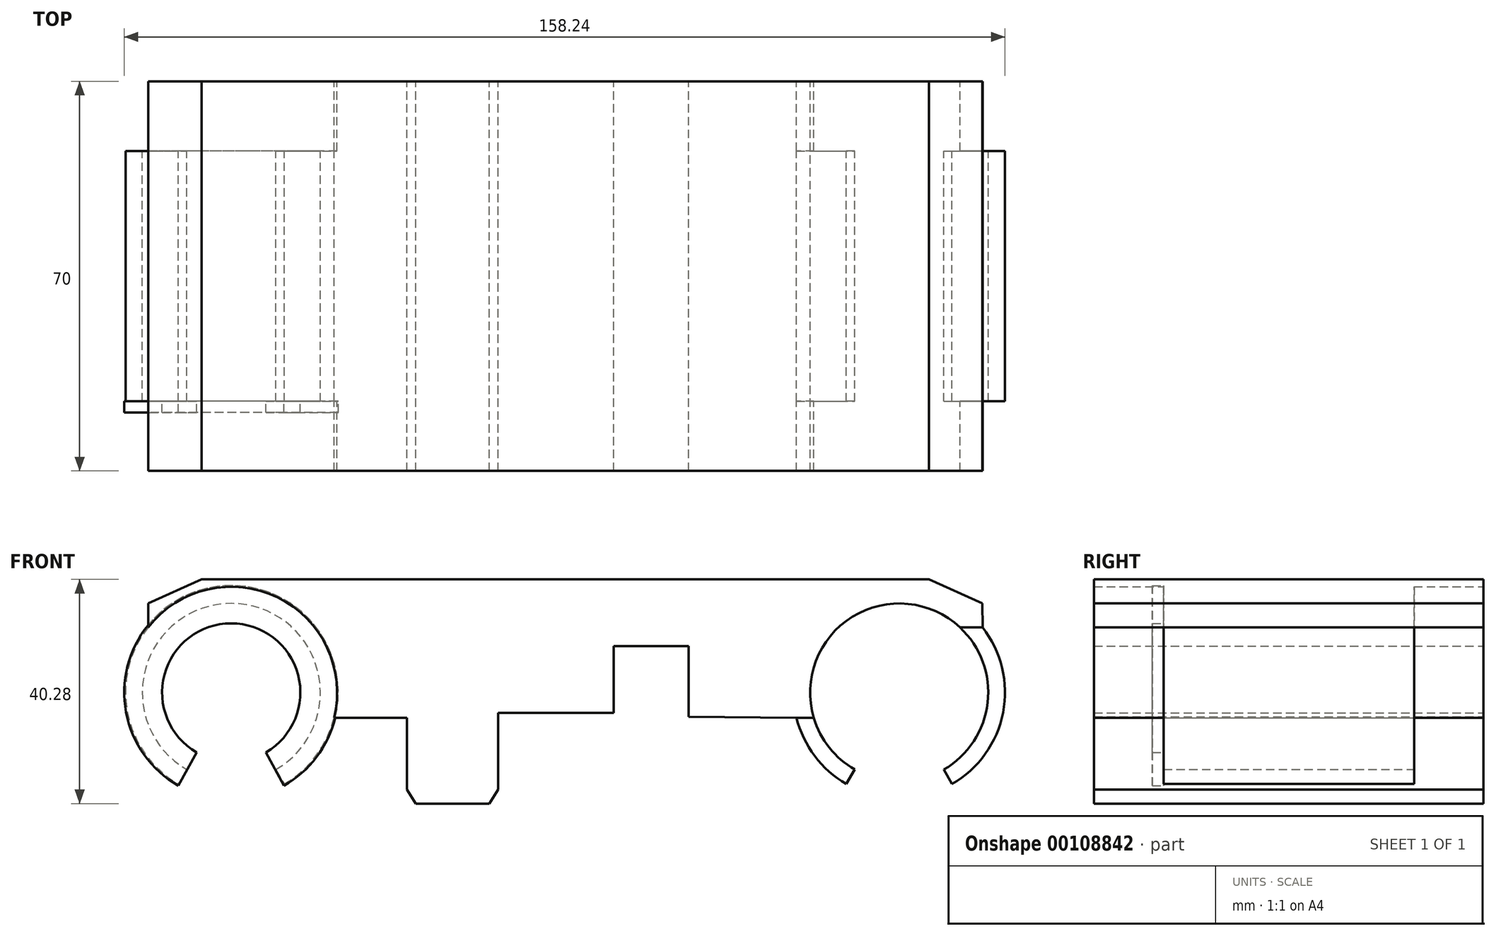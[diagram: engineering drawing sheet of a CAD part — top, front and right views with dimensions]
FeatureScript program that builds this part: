
annotation { "Feature Type Name" : "Feature", "Feature Type Description" : "" }
export const myFeature = defineFeature(function(context is Context, id is Id, definition is map)
    precondition{}
    {
        {
            var Q0;
            Q0=qCreatedBy(makeId("Front.planeOp"),FACE);
            var sketch = newSketch(context, id + "F0", { "sketchPlane" : qUnion([Q0])});
            skLineSegment(sketch, "E0", {"start": v(-86.21, 0) * mm, "end": v(92.3, 0) * mm, "construction": true});
            skLineSegment(sketch, "E1", {"start": v(0, 52.83) * mm, "end": v(0, -43) * mm, "construction": true});
            skLineSegment(sketch, "E2", {"start": v(-60, 31.81) * mm, "end": v(-60, -33) * mm, "construction": true});
            skLineSegment(sketch, "E3", {"start": v(60, 36.92) * mm, "end": v(60, -41.44) * mm, "construction": true});
            skLineSegment(sketch, "E4", {"start": v(-113.9, -4.57) * mm, "end": v(-28.43, -4.57) * mm, "construction": true});
            skArc(sketch, "E5", {"start": v(-52, -13.86) * mm, "mid": v(-60, 16) * mm, "end": v(-68, -13.86) * mm});
            skArc(sketch, "E6", {"start": v(68, -13.86) * mm, "mid": v(60, 16) * mm, "end": v(52, -13.86) * mm});
            skArc(sketch, "E7", {"start": v(-74.95, 11.72) * mm, "mid": v(-78.65, -3.6) * mm, "end": v(-69.5, -16.45) * mm});
            skArc(sketch, "E8", {"start": v(69.5, -16.45) * mm, "mid": v(78.65, -3.63) * mm, "end": v(74.98, 11.7) * mm});
            skLineSegment(sketch, "E9", {"start": v(-68, -13.86) * mm, "end": v(-69.5, -16.45) * mm});
            skLineSegment(sketch, "E10.MirrorCS", {"start": v(-52, -13.86) * mm, "end": v(-50.5, -16.45) * mm});
            skLineSegment(sketch, "E11.MirrorCS", {"start": v(68, -13.86) * mm, "end": v(69.5, -16.45) * mm});
            skLineSegment(sketch, "E12.MirrorCS", {"start": v(-60, 36.92) * mm, "end": v(-60, -41.44) * mm, "construction": true});
            skLineSegment(sketch, "E13.MirrorCS", {"start": v(52, -13.86) * mm, "end": v(50.5, -16.45) * mm});
            skLineSegment(sketch, "E14", {"start": v(-41.56, -4.57) * mm, "end": v(-28.43, -4.57) * mm});
            skLineSegment(sketch, "E15", {"start": v(-74.95, 11.72) * mm, "end": v(-74.95, 16.02) * mm});
            skLineSegment(sketch, "E16", {"start": v(65.33, 20.32) * mm, "end": v(-65.33, 20.32) * mm});
            skArc(sketch, "E17.trimOffspring", {"start": v(-50.5, -16.45) * mm, "mid": v(-44.82, -11.42) * mm, "end": v(-41.56, -4.57) * mm});
            skArc(sketch, "E18.trimOffspring", {"start": v(41.56, -4.57) * mm, "mid": v(44.82, -11.42) * mm, "end": v(50.5, -16.45) * mm});
            skLineSegment(sketch, "E19", {"start": v(74.98, 11.7) * mm, "end": v(70.92, 11.7) * mm});
            skLineSegment(sketch, "E20", {"start": v(44.67, -4.57) * mm, "end": v(41.56, -4.57) * mm});
            skLineSegment(sketch, "E21", {"start": v(-41.56, -4.57) * mm, "end": v(-44.67, -4.57) * mm});
            skLineSegment(sketch, "E22", {"start": v(-74.95, 11.72) * mm, "end": v(-70.89, 11.72) * mm});
            skLineSegment(sketch, "E23", {"start": v(-74.95, 16.02) * mm, "end": v(-65.33, 20.32) * mm});
            skLineSegment(sketch, "E24.MirrorCS", {"start": v(74.95, 16.02) * mm, "end": v(65.33, 20.32) * mm});
            skPoint(sketch, "E25.orphan", {"position": v(-74.95, 20.32) * mm});
            skLineSegment(sketch, "E26", {"start": v(74.98, 11.7) * mm, "end": v(74.95, 16.02) * mm});
            skArc(sketch, "E27", {"start": v(-50.5, -16.45) * mm, "mid": v(-60, 19) * mm, "end": v(-69.5, -16.45) * mm});
            skArc(sketch, "E28", {"start": v(-53.75, -10.83) * mm, "mid": v(-60, 12.5) * mm, "end": v(-66.25, -10.83) * mm});
            skLineSegment(sketch, "E29", {"start": v(-69.5, -16.45) * mm, "end": v(-66.25, -10.83) * mm});
            skLineSegment(sketch, "E30", {"start": v(-53.75, -10.83) * mm, "end": v(-50.5, -16.45) * mm});
            skLineSegment(sketch, "E31", {"start": v(22.18, -4.34) * mm, "end": v(22.18, 8.35) * mm});
            skLineSegment(sketch, "E32", {"start": v(22.18, 8.35) * mm, "end": v(8.67, 8.35) * mm});
            skLineSegment(sketch, "E33", {"start": v(8.67, 8.35) * mm, "end": v(8.67, -3.66) * mm});
            skLineSegment(sketch, "E34", {"start": v(-28.43, -4.57) * mm, "end": v(-28.43, -17.45) * mm});
            skLineSegment(sketch, "E35", {"start": v(-26.86, -19.96) * mm, "end": v(-13.63, -19.96) * mm});
            skLineSegment(sketch, "E36.trimOffspring", {"start": v(41.56, -4.57) * mm, "end": v(102.9, -4.57) * mm, "construction": true});
            skLineSegment(sketch, "E37", {"start": v(22.18, -4.34) * mm, "end": v(41.56, -4.57) * mm});
            skLineSegment(sketch, "E38", {"start": v(-28.7, -3.66) * mm, "end": v(13.04, -3.66) * mm, "construction": true});
            skLineSegment(sketch, "E39", {"start": v(-12.06, -3.63) * mm, "end": v(-12.06, -25.4) * mm, "construction": true});
            skLineSegment(sketch, "E40", {"start": v(8.67, -3.66) * mm, "end": v(-12.06, -3.66) * mm});
            skLineSegment(sketch, "E41", {"start": v(-12.06, -3.66) * mm, "end": v(-12.06, -17.45) * mm});
            skLineSegment(sketch, "E42", {"start": v(-12.06, -17.45) * mm, "end": v(-13.63, -19.96) * mm});
            skLineSegment(sketch, "E43", {"start": v(-12.06, -17.45) * mm, "end": v(-28.43, -17.45) * mm, "construction": true});
            skLineSegment(sketch, "E44", {"start": v(-28.43, -17.45) * mm, "end": v(-26.86, -19.96) * mm});
            skSolve(sketch);
        }
        {
            var Q0;
            Q0=makeQuery(id+"F0.imprint","IMPRINT",FACE,{"disambiguationData":[TD([[makeQuery(id+"F0.imprint","IMPRINT",EDGE,{"derivedFrom":sQuery(id+"F0.wireOp",EDGE,"E14")}),1.0]])]});
            extrude(context, id + "F1", {"entities" : qUnion([Q0]), "endBound" : BoundingType.SYMMETRIC, "depth" : 70 * mm});
        }
        {
            var Q0;
            {var subQ3=sQuery(id+"F0.wireOp",EDGE,"E22");Q0=makeQuery(id+"F0.imprint","IMPRINT",FACE,{"disambiguationData":[TD([[makeQuery(id+"F0.imprint","IMPRINT",EDGE,{"derivedFrom":subQ3}),-1.0]])]});}
            var Q1;
            {var subQ3=sQuery(id+"F0.wireOp",EDGE,"E21");Q1=makeQuery(id+"F0.imprint","IMPRINT",FACE,{"disambiguationData":[TD([[makeQuery(id+"F0.imprint","IMPRINT",EDGE,{"derivedFrom":subQ3}),1.0]])]});}
            var Q2;
            {var subQ0=sQuery(id+"F0.wireOp",EDGE,"E21");Q2=makeQuery(id+"F0.imprint","IMPRINT",FACE,{"disambiguationData":[TD([[makeQuery(id+"F0.imprint","IMPRINT",EDGE,{"derivedFrom":subQ0}),-1.0]])]});}
            var Q3;
            {var subQ0=sQuery(id+"F0.wireOp",EDGE,"E13.MirrorCS");Q3=makeQuery(id+"F0.imprint","IMPRINT",FACE,{"disambiguationData":[TD([[makeQuery(id+"F0.imprint","IMPRINT",EDGE,{"derivedFrom":subQ0}),-1.0]])]});}
            var Q4;
            Q4=makeQuery(id+"F0.imprint","IMPRINT",FACE,{"disambiguationData":[TD([[makeQuery(id+"F0.imprint","IMPRINT",EDGE,{"derivedFrom":sQuery(id+"F0.wireOp",EDGE,"E8")}),1.0]])]});
            extrude(context, id + "F2", {"entities" : qUnion([Q0, Q1, Q2, Q3, Q4]), "operationType" : NewBodyOperationType.ADD, "endBound" : BoundingType.SYMMETRIC, "depth" : 45 * mm});
        }
        {
            var Q0;
            Q0=makeQuery(id+"F2.opExtrude","CAP_FACE",FACE,{"disambiguationData":[OSD([sQuery(id+"F0.wireOp",EDGE,"E5"),sQuery(id+"F0.wireOp",EDGE,"E27"),sQuery(id+"F0.wireOp",EDGE,"E29"),sQuery(id+"F0.wireOp",EDGE,"E30")])],"isStart":false});
            cPlane(context, id + "F3", {"entities" : qUnion([Q0]), "cplaneType" : CPlaneType.OFFSET, "offset" : 0 * mm, "width" : 150 * mm, "height" : 150 * mm});
        }
        {
            var Q0;
            Q0=qCreatedBy(id+"F3.planeOp",FACE);
            var sketch = newSketch(context, id + "F4", { "sketchPlane" : qUnion([Q0])});
            skArc(sketch, "E45", {"start": v(-53.8, -10.76) * mm, "mid": v(-60.02, 12.43) * mm, "end": v(-66.23, -10.76) * mm});
            skArc(sketch, "E46", {"start": v(-50.56, -16.74) * mm, "mid": v(-60, 19.23) * mm, "end": v(-69.51, -16.72) * mm});
            skLineSegment(sketch, "E47", {"start": v(-69.51, -16.72) * mm, "end": v(-66.23, -10.76) * mm});
            skLineSegment(sketch, "E48", {"start": v(-50.56, -16.74) * mm, "end": v(-53.8, -10.76) * mm});
            skArc(sketch, "E49.MirrorCS", {"start": v(50.56, -16.74) * mm, "mid": v(60, 19.23) * mm, "end": v(69.51, -16.72) * mm});
            skArc(sketch, "E50.MirrorCS", {"start": v(53.8, -10.76) * mm, "mid": v(60.02, 12.43) * mm, "end": v(66.23, -10.76) * mm});
            skLineSegment(sketch, "E51.MirrorCS", {"start": v(50.56, -16.74) * mm, "end": v(53.8, -10.76) * mm});
            skLineSegment(sketch, "E52.MirrorCS", {"start": v(69.51, -16.72) * mm, "end": v(66.23, -10.76) * mm});
            skSolve(sketch);
        }
        {
            var Q0;
            Q0=makeQuery(id+"F4.imprint","IMPRINT",FACE,{"disambiguationData":[TD([[makeQuery(id+"F4.imprint","IMPRINT",EDGE,{"derivedFrom":sQuery(id+"F4.wireOp",EDGE,"E45")}),-1.0]])]});
            var Q1;
            Q1=makeQuery(id+"F4.imprint","IMPRINT",FACE,{"disambiguationData":[TD([[makeQuery(id+"F4.imprint","IMPRINT",EDGE,{"derivedFrom":sQuery(id+"F4.wireOp",EDGE,"E49.MirrorCS")}),-1.0]])]});
            extrude(context, id + "F5", {"entities" : qUnion([Q0, Q1]), "depth" : 2 * mm});
        }
        {
            var Q0;
            Q0=makeQuery(id+"F1.opExtrude","SWEPT_FACE",FACE,{"disambiguationData":[OSD([sQuery(id+"F0.wireOp",EDGE,"E41")])]});
            var sketch = newSketch(context, id + "F6", { "sketchPlane" : qUnion([Q0])});
            skLineSegment(sketch, "E53", {"start": v(-33.91, -11.91) * mm, "end": v(35.17, -11.91) * mm, "construction": true});
            skLineSegment(sketch, "E54", {"start": v(20, -6.48) * mm, "end": v(20, -13.5) * mm, "construction": true});
            skLineSegment(sketch, "E55.MirrorCS", {"start": v(-20, -6.48) * mm, "end": v(-20, -13.5) * mm, "construction": true});
            skPoint(sketch, "E56", {"position": v(-20, -11.91) * mm});
            skPoint(sketch, "E57", {"position": v(20, -11.91) * mm});
            skLineSegment(sketch, "E58", {"start": v(-35, -6.06) * mm, "end": v(-35, -13.52) * mm, "construction": true});
            skLineSegment(sketch, "E59", {"start": v(35, -14.26) * mm, "end": v(35, -5.66) * mm, "construction": true});
            skSolve(sketch);
        }
        {
            var Q0;
            Q0=sQuery(id+"F6.wireOp",VERTEX,"E56");
            var Q1;
            Q1=sQuery(id+"F6.wireOp",VERTEX,"E57");
            var Q2;
            Q2=makeQuery(id+"F5.opExtrude","SWEPT_BODY",BODY,{"disambiguationData":[OSD([sQuery(id+"F4.wireOp",EDGE,"E45"),sQuery(id+"F4.wireOp",EDGE,"E46"),sQuery(id+"F4.wireOp",EDGE,"E47"),sQuery(id+"F4.wireOp",EDGE,"E48")])]});
            hole(context, id + "F7", {"style" : HoleStyle.SIMPLE, "endStyle" : HoleEndStyle.BLIND, "standardTappedOrClearance" : lookupTablePath({ "standard" : "ISO", "size" : "2.4", "type" : "Drilled" }), "standardBlindInLast" : lookupTablePath({ "standard" : "ISO", "size" : "2.4", "type" : "Drilled" }), "holeDiameter" : 2.4 * mm, "holeDepth" : 18 * mm, "startFromSketch" : true, "locations" : qUnion([Q0, Q1]), "scope" : qUnion([Q2])});
        }
        {
            var Q0;
            Q0=makeQuery(id+"F1.opExtrude","SWEPT_FACE",FACE,{"disambiguationData":[OSD([sQuery(id+"F0.wireOp",EDGE,"E16")])]});
            cPlane(context, id + "F8", {"entities" : qUnion([Q0]), "cplaneType" : CPlaneType.OFFSET, "offset" : 0 * mm, "width" : 150 * mm, "height" : 150 * mm});
        }
        {
            var Q0;
            Q0=qCreatedBy(id+"F8.planeOp",FACE);
            var sketch = newSketch(context, id + "F9", { "sketchPlane" : qUnion([Q0])});
            skPoint(sketch, "E60", {"position": v(0, 0) * mm});
            skSolve(sketch);
        }
        {
            var Q0;
            Q0=sQuery(id+"F9.wireOp",VERTEX,"E60");
            var Q1;
            Q1=makeQuery(id+"F5.opExtrude","SWEPT_BODY",BODY,{"disambiguationData":[OSD([sQuery(id+"F4.wireOp",EDGE,"E45"),sQuery(id+"F4.wireOp",EDGE,"E46"),sQuery(id+"F4.wireOp",EDGE,"E47"),sQuery(id+"F4.wireOp",EDGE,"E48")])]});
            hole(context, id + "F10", {"style" : HoleStyle.SIMPLE, "endStyle" : HoleEndStyle.THROUGH, "standardTappedOrClearance" : lookupTablePath({ "standard" : "ISO", "size" : "5", "type" : "Drilled" }), "standardBlindInLast" : lookupTablePath({ "standard" : "ISO", "size" : "5", "type" : "Drilled" }), "holeDiameter" : 5 * mm, "startFromSketch" : true, "locations" : qUnion([Q0]), "scope" : qUnion([Q1]), "isTappedThrough" : true});
        }
    });
